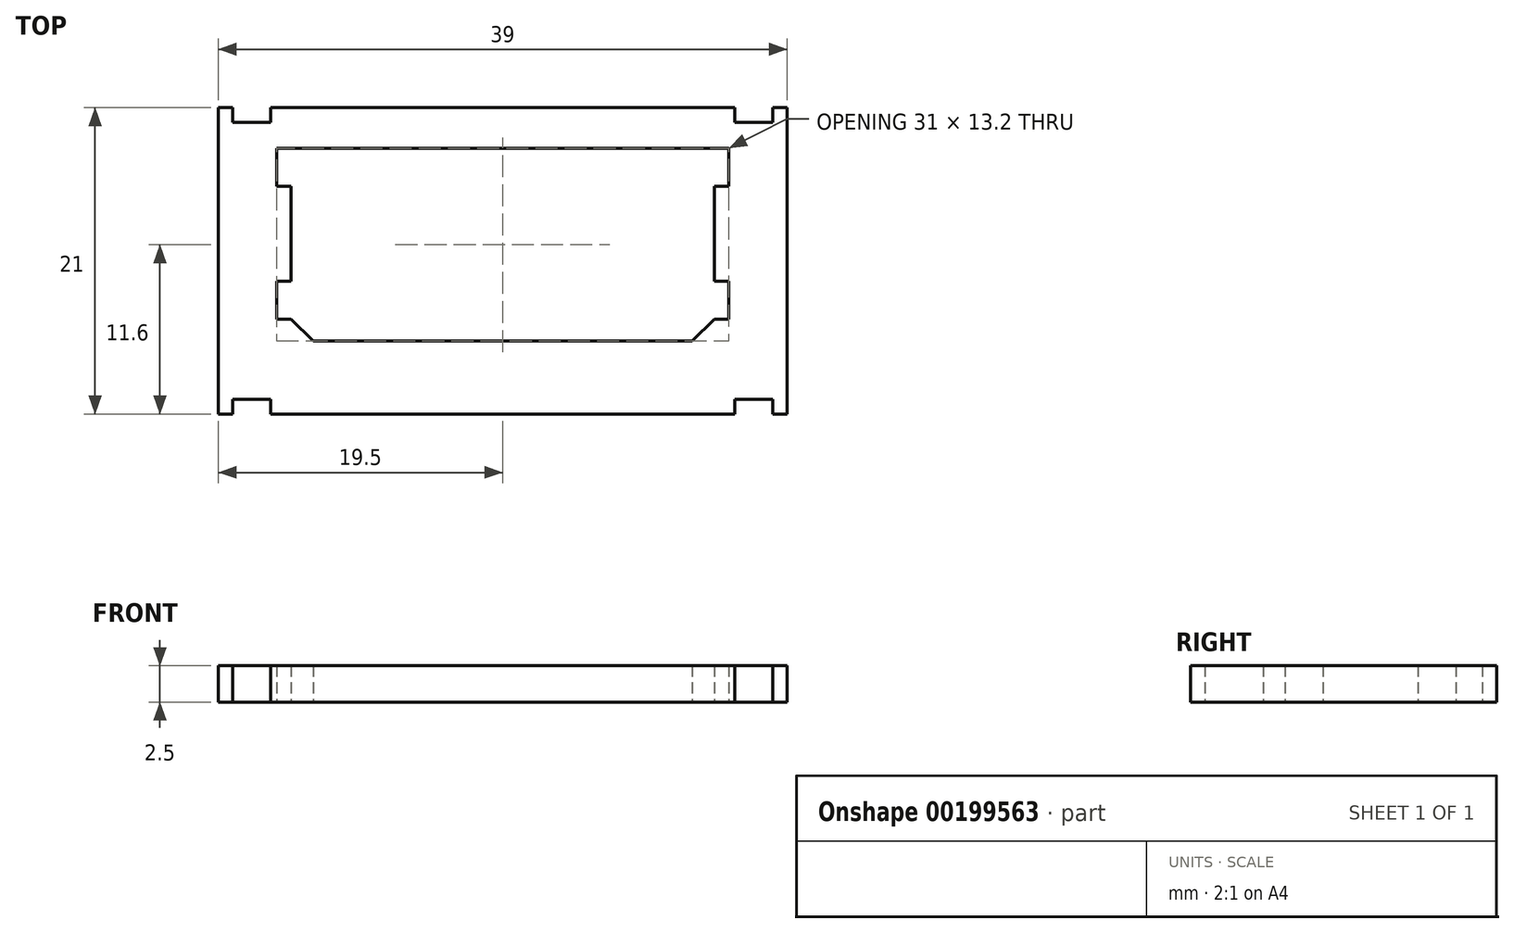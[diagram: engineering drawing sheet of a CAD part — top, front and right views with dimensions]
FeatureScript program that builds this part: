
annotation { "Feature Type Name" : "Feature", "Feature Type Description" : "" }
export const myFeature = defineFeature(function(context is Context, id is Id, definition is map)
    precondition{}
    {
        {
            var Q0;
            Q0=qCreatedBy(makeId("Top.planeOp"),FACE);
            var sketch = newSketch(context, id + "F0", { "sketchPlane" : qUnion([Q0])});
            skLineSegment(sketch, "E0.bottom", {"start": v(19.5, -10.5) * mm, "end": v(18.5, -10.5) * mm});
            skLineSegment(sketch, "E0.top", {"start": v(19.5, 10.5) * mm, "end": v(18.5, 10.5) * mm});
            skLineSegment(sketch, "E0.left", {"start": v(19.5, -10.5) * mm, "end": v(19.5, 10.5) * mm});
            skLineSegment(sketch, "E0.right", {"start": v(-19.5, -10.5) * mm, "end": v(-19.5, 10.5) * mm});
            skPoint(sketch, "E0.middle", {"position": v(0, 0) * mm});
            skLineSegment(sketch, "E1", {"start": v(-14.5, 5.1) * mm, "end": v(-14.5, -1.4) * mm});
            skLineSegment(sketch, "E2", {"start": v(-18.5, 9.5) * mm, "end": v(-15.9, 9.5) * mm});
            skLineSegment(sketch, "E3", {"start": v(-18.5, -9.5) * mm, "end": v(-15.9, -9.5) * mm});
            skLineSegment(sketch, "E4", {"start": v(-18.5, 10.5) * mm, "end": v(-18.5, 9.5) * mm});
            skLineSegment(sketch, "E5", {"start": v(18.5, 10.5) * mm, "end": v(18.5, 9.5) * mm});
            skLineSegment(sketch, "E6", {"start": v(-15.9, 10.5) * mm, "end": v(-15.9, 9.5) * mm});
            skLineSegment(sketch, "E7", {"start": v(15.9, 10.5) * mm, "end": v(15.9, 9.5) * mm});
            skLineSegment(sketch, "E8", {"start": v(-13, -5.5) * mm, "end": v(13, -5.5) * mm});
            skLineSegment(sketch, "E9", {"start": v(-15.5, 7.7) * mm, "end": v(-15.5, 5.1) * mm});
            skLineSegment(sketch, "E10", {"start": v(15.5, 7.7) * mm, "end": v(15.5, 5.1) * mm});
            skLineSegment(sketch, "E11", {"start": v(14.5, 5.1) * mm, "end": v(14.5, -1.4) * mm});
            skLineSegment(sketch, "E12", {"start": v(15.5, -4) * mm, "end": v(14.5, -4) * mm});
            skLineSegment(sketch, "E13.trimOffspring", {"start": v(-18.5, -10.5) * mm, "end": v(-19.5, -10.5) * mm});
            skLineSegment(sketch, "E14.trimOffspring", {"start": v(-18.5, -9.5) * mm, "end": v(-18.5, -10.5) * mm});
            skLineSegment(sketch, "E15.trimOffspring", {"start": v(-15.9, -9.5) * mm, "end": v(-15.9, -10.5) * mm});
            skLineSegment(sketch, "E16.trimOffspring", {"start": v(15.9, -9.5) * mm, "end": v(18.5, -9.5) * mm});
            skLineSegment(sketch, "E17.trimOffspring", {"start": v(18.5, -9.5) * mm, "end": v(18.5, -10.5) * mm});
            skLineSegment(sketch, "E18.trimOffspring", {"start": v(15.9, -9.5) * mm, "end": v(15.9, -10.5) * mm});
            skLineSegment(sketch, "E19.trimOffspring", {"start": v(15.9, 9.5) * mm, "end": v(18.5, 9.5) * mm});
            skLineSegment(sketch, "E20.trimOffspring", {"start": v(-18.5, 10.5) * mm, "end": v(-19.5, 10.5) * mm});
            skLineSegment(sketch, "E21.trimOffspring", {"start": v(15.9, 10.5) * mm, "end": v(-15.9, 10.5) * mm});
            skLineSegment(sketch, "E22.trimOffspring", {"start": v(15.9, -10.5) * mm, "end": v(-15.9, -10.5) * mm});
            skLineSegment(sketch, "E23", {"start": v(-15.5, 7.7) * mm, "end": v(15.5, 7.7) * mm});
            skLineSegment(sketch, "E24", {"start": v(-15.5, 5.1) * mm, "end": v(-14.5, 5.1) * mm});
            skLineSegment(sketch, "E25", {"start": v(-15.5, -1.4) * mm, "end": v(-14.5, -1.4) * mm});
            skLineSegment(sketch, "E26.trimOffspring", {"start": v(-15.5, -1.4) * mm, "end": v(-15.5, -4) * mm});
            skLineSegment(sketch, "E27.trimOffspring", {"start": v(15.5, -1.4) * mm, "end": v(15.5, -4) * mm});
            skLineSegment(sketch, "E28.trimOffspring", {"start": v(14.5, -1.4) * mm, "end": v(15.5, -1.4) * mm});
            skLineSegment(sketch, "E29.trimOffspring", {"start": v(14.5, 5.1) * mm, "end": v(15.5, 5.1) * mm});
            skLineSegment(sketch, "E30.trimOffspring", {"start": v(-14.5, -4) * mm, "end": v(-15.5, -4) * mm});
            skLineSegment(sketch, "E31", {"start": v(14.5, -4) * mm, "end": v(13, -5.5) * mm});
            skPoint(sketch, "E32", {"position": v(-13, -5.5) * mm});
            skLineSegment(sketch, "E33", {"start": v(-14.5, -4) * mm, "end": v(-13, -5.5) * mm});
            skSolve(sketch);
        }
        {
            var Q0;
            Q0=makeQuery(id+"F0.imprint","IMPRINT",FACE,{"disambiguationData":[TD([[makeQuery(id+"F0.imprint","IMPRINT",EDGE,{"derivedFrom":sQuery(id+"F0.wireOp",EDGE,"E0.bottom")}),-1.0]])]});
            extrude(context, id + "F1", {"entities" : qUnion([Q0]), "depth" : 2.5 * mm});
        }
    });
